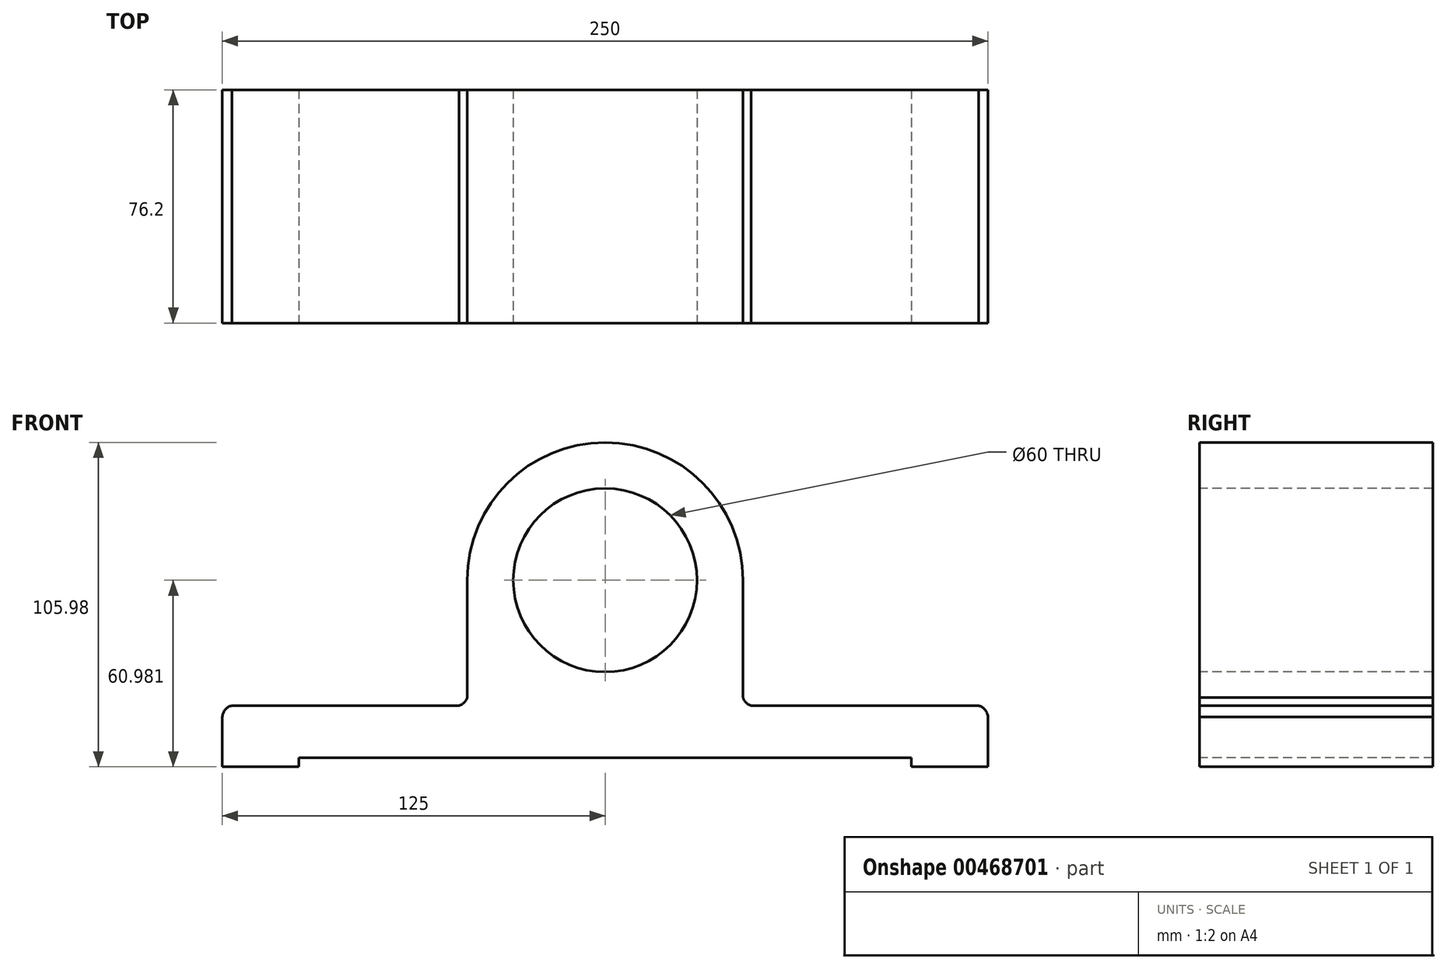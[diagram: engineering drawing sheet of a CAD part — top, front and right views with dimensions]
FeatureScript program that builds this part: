
annotation { "Feature Type Name" : "Feature", "Feature Type Description" : "" }
export const myFeature = defineFeature(function(context is Context, id is Id, definition is map)
    precondition{}
    {
        {
            var Q0;
            Q0=qCreatedBy(makeId("Front.planeOp"),FACE);
            var sketch = newSketch(context, id + "F0", { "sketchPlane" : qUnion([Q0])});
            skArc(sketch, "E0", {"start": v(45, 41.17) * mm, "mid": v(0, 86.17) * mm, "end": v(-45, 41.17) * mm});
            skCircle(sketch, "E1", {"center": v(0, 41.17) * mm, "radius": 30 * mm});
            skLineSegment(sketch, "E2", {"start": v(-45, 41.17) * mm, "end": v(-45, 2.9) * mm});
            skArc(sketch, "E3", {"start": v(-47.7, 0.2) * mm, "mid": v(-46, 1.2) * mm, "end": v(-45, 2.9) * mm});
            skLineSegment(sketch, "E4.trimOffspring", {"start": v(-47.7, 0.2) * mm, "end": v(-121.91, 0.2) * mm});
            skLineSegment(sketch, "E5", {"start": v(-125, -3.45) * mm, "end": v(-125, -19.8) * mm});
            skLineSegment(sketch, "E6", {"start": v(-125, -19.8) * mm, "end": v(-100, -19.8) * mm});
            skLineSegment(sketch, "E7", {"start": v(-100, -19.8) * mm, "end": v(-100, -16.8) * mm});
            skLineSegment(sketch, "E8", {"start": v(-100, -16.8) * mm, "end": v(0, -16.8) * mm});
            skLineSegment(sketch, "E9.MirrorCS", {"start": v(45, 41.17) * mm, "end": v(45, 2.9) * mm});
            skArc(sketch, "E10.MirrorCS", {"start": v(47.7, 0.2) * mm, "mid": v(46, 1.2) * mm, "end": v(45, 2.9) * mm});
            skLineSegment(sketch, "E11.MirrorCS", {"start": v(47.7, 0.2) * mm, "end": v(121.91, 0.2) * mm});
            skLineSegment(sketch, "E12.MirrorCS", {"start": v(125, -3.45) * mm, "end": v(125, -19.8) * mm});
            skLineSegment(sketch, "E13.MirrorCS", {"start": v(125, -19.8) * mm, "end": v(100, -19.8) * mm});
            skLineSegment(sketch, "E14.MirrorCS", {"start": v(100, -16.8) * mm, "end": v(0, -16.8) * mm});
            skLineSegment(sketch, "E15.MirrorCS", {"start": v(100, -19.8) * mm, "end": v(100, -16.8) * mm});
            skArc(sketch, "E16", {"start": v(125, -3.45) * mm, "mid": v(124.06, -1.12) * mm, "end": v(121.91, 0.2) * mm});
            skPoint(sketch, "E17.orphan", {"position": v(125, 0.2) * mm});
            skArc(sketch, "E18.MirrorCS", {"start": v(-125, -3.45) * mm, "mid": v(-124.06, -1.12) * mm, "end": v(-121.91, 0.2) * mm});
            skSolve(sketch);
        }
        {
            var Q0;
            Q0=makeQuery(id+"F0.imprint","IMPRINT",FACE,{"disambiguationData":[TD([[makeQuery(id+"F0.imprint","IMPRINT",EDGE,{"derivedFrom":sQuery(id+"F0.wireOp",EDGE,"E0")}),1.0]])]});
            extrude(context, id + "F1", {"entities" : qUnion([Q0]), "oppositeDirection" : true, "depth" : 76.2 * mm});
        }
    });
